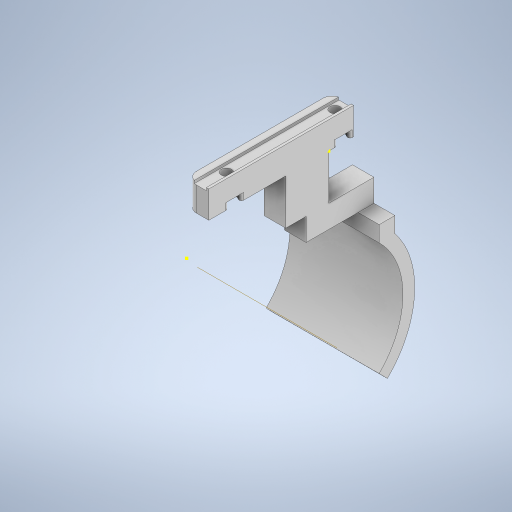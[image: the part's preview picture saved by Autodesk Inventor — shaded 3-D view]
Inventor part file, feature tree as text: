
AUTODESK INVENTOR PART (.ipt)
format: ipt  version: 2024 (Build 280153000, 153)  size: 397,312 bytes
history: native  units: in
note: dims shown in document units (in); Inventor stores cm internally (conversion verified against a paired STEP export)
features: sketch x12, extrude x7, projected_geometry x4, fillet x2, sweep x1, other x1, revolve x1
ambient origin geometry x8: Origin, YZ Plane, XZ Plane, XY Plane, X Axis, Y Axis, Z Axis, Center Point
bodies: Solid1 (feature_tree)
feature tree (28):
  extrude  "Extrusion1"  Depth=2.5197in
  extrude  "Extrusion2"  Depth=1.8898in
  extrude  "Extrusion3"  Depth=0.4724in TaperAngle=0.0deg
  fillet  "Fillet1"  Radius=0.0433in
  fillet  "Fillet2"  Radius=0.2126in
  extrude  "Extrusion19"  Depth=0.4724in TaperAngle=0.0deg
  extrude  "Extrusion21"  Depth=0.1181in TaperAngle=0.0deg
  sketch  "Sketch41"  dims[d17=0.1772in d18=0.0394in]
  extrude  "Extrusion22"  Depth=0.0394in
  sweep  "Sweep3"
  extrude  "Extrusion23"  Depth=0.748in
  sketch  "Sketch47"  dims[d132=0.3937in d133=0.0in]
  other  "Work Axis2"
  revolve  "Revolution2"  [1 undecoded]
  sketch  "Sketch48"  dims[d134=1.2283in d135=180.0deg d136=0.2756in d137=1.9685in d138=0.2756in d139=0.2756in d140=0.0in d141=1.9685in d142=1.378in d143=0.0in d144=0.0in d147=0.3937in d148=0.0in d149=0.0787in d150=90.0deg d42=0.0197in d43=0.0344in d44=0.0197in d45=0.0344in d46=0.0in d47=0.0in d48=0.0in d49=0.0in d50=0.0in d51=0.0in d52=0.0in d53=0.0in d55=0.0197in d56=0.0344in d57=0.0197in d58=0.0344in d60=0.0197in d61=0.0344in d62=0.0197in d63=0.0344in d72=0.0197in d73=0.0344in d74=0.0197in d75=0.0344in]
  sketch  "Sketch1"  dims[d1=0.374in d2=2.5197in]
  sketch  "Sketch2"  dims[d3=0.1772in d4=1.8898in]
  sketch  "Sketch3"  dims[d6=0.1457in d7=0.4724in d8=0.0in d9=0.0433in d10=0.2126in]
  projected_geometry  "Projected Loop2"
  projected_geometry  "Projected Loop3"
  projected_geometry  "Projected Loop4"
  projected_geometry  "Projected Loop5"
  sketch  "Sketch28"  dims[d11=0.0472in d12=0.4724in d13=0.0in]
  sketch  "Sketch40"  dims[d14=0.2953in d15=0.1181in d16=0.0in]
  sketch  "Sketch42"  dims[d19=0.1575in d76=0.4724in]
  sketch  "Sketch43"  dims[d107=0.102in d108=0.748in]
  sketch  "Sketch44"  dims[d109=0.7874in d110=0.0in d130=0.7874in]
  sketch  "Sketch46"  dims[d131=1.1811in]
note: 1 required parameter value undecoded (feature->parameter linkage not recoverable at this tier; creation-order binding heuristic only, values carry confidence <= 0.55)
